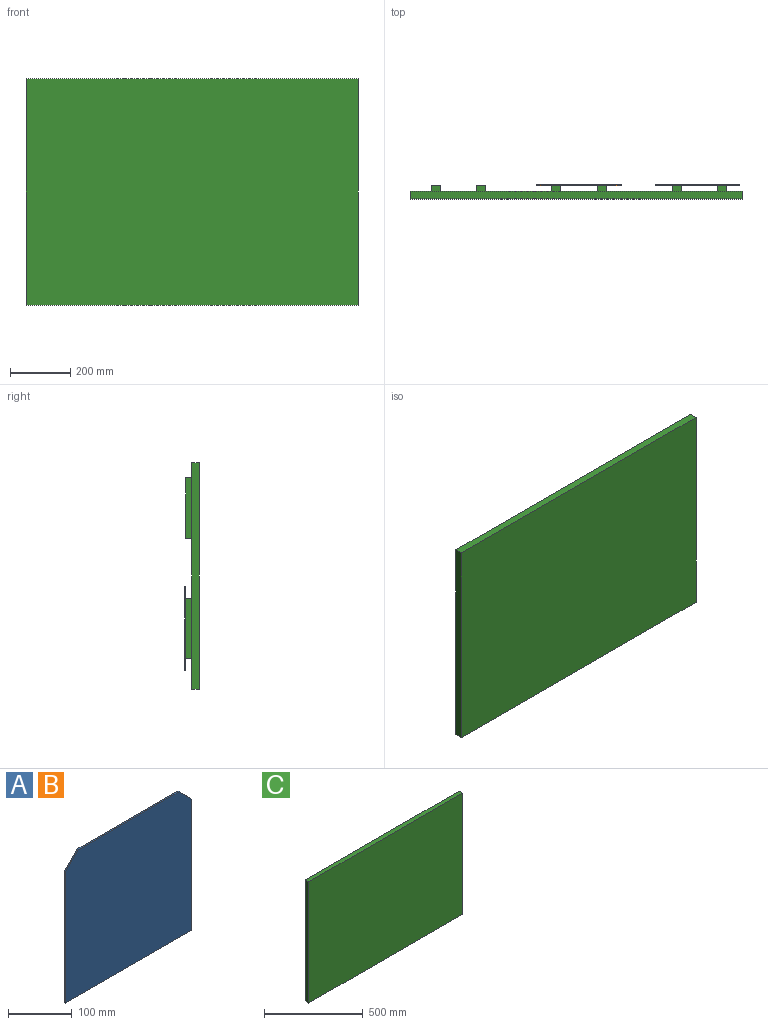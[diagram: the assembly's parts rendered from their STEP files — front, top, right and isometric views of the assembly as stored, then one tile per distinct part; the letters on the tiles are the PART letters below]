
ASSEMBLY  parts=3 mates=2
PART A: 8 faces, bbox 280x3x280 mm
  f0: plane 280x3mm, normal (0,0,-1), area 840mm2, adj f1,f5,f6,f7
  f1: plane 251.72x3mm, normal (1,0,0), area 755.1mm2, adj f0,f2,f6,f7
  f2: plane 28.28x28.28mm, normal (0.71,0,0.71), area 120mm2, adj f1,f3,f6,f7
  f3: plane 223.43x3mm, normal (0,0,1), area 670.3mm2, adj f2,f4,f6,f7
  f4: plane 28.28x28.28mm, normal (-0.71,0,0.71), area 120mm2, adj f3,f5,f6,f7
  f5: plane 251.72x3mm, normal (-1,0,0), area 755.1mm2, adj f0,f4,f6,f7
  f6: plane 280x280mm, normal (0,-1,0), area 77600mm2, adj f0,f1,f2,f3,f4,f5
  f7: plane 280x280mm, normal (0,1,0), area 77600mm2, adj f0,f1,f2,f3,f4,f5
PART B: same geometry as A
PART C: 66 faces, bbox 1100x45x750 mm
  f0: plane 200x20mm, normal (1,0,0), area 4000mm2, adj f1,f3,f4,f10
  f1: plane 30x20mm, normal (0,0,-1), area 600mm2, adj f0,f2,f4,f10
  f2: plane 200x20mm, normal (-1,0,0), area 4000mm2, adj f1,f3,f4,f10
  f3: plane 30x20mm, normal (0,0,1), area 600mm2, adj f0,f2,f4,f10
  f4: plane 200x30mm, normal (0,1,0), area 6000mm2, adj f0,f1,f2,f3
  f5: plane 750x25mm, normal (-1,0,0), area 18750mm2, adj f6,f8,f9,f10
  f6: plane 1100x25mm, normal (0,0,-1), area 27500mm2, adj f5,f7,f9,f10
  f7: plane 750x25mm, normal (1,0,0), area 18750mm2, adj f6,f8,f9,f10
  f8: plane 1100x25mm, normal (0,0,1), area 27500mm2, adj f5,f7,f9,f10
  f9: plane 1100x750mm, normal (0,-1,0), area 825000mm2, adj f5,f6,f7,f8
  f10: plane 1100x750mm, normal (0,1,0), area 753000mm2, adj f0,f1,f2,f3,f5,f6,f7,f8
  f11: plane 200x20mm, normal (1,0,0), area 4000mm2, adj f10,f12,f14,f15
  f12: plane 30x20mm, normal (0,0,-1), area 600mm2, adj f10,f11,f13,f15
  f13: plane 200x20mm, normal (-1,0,0), area 4000mm2, adj f10,f12,f14,f15
  f14: plane 30x20mm, normal (0,0,1), area 600mm2, adj f10,f11,f13,f15
  f15: plane 200x30mm, normal (0,1,0), area 6000mm2, adj f11,f12,f13,f14
  f16: plane 200x20mm, normal (1,0,0), area 4000mm2, adj f10,f17,f19,f20
  f17: plane 30x20mm, normal (0,0,-1), area 600mm2, adj f10,f16,f18,f20
  f18: plane 200x20mm, normal (-1,0,0), area 4000mm2, adj f10,f17,f19,f20
  f19: plane 30x20mm, normal (0,0,1), area 600mm2, adj f10,f16,f18,f20
  f20: plane 200x30mm, normal (0,1,0), area 6000mm2, adj f16,f17,f18,f19
  f21: plane 200x20mm, normal (1,0,0), area 4000mm2, adj f10,f22,f24,f25
  f22: plane 30x20mm, normal (0,0,-1), area 600mm2, adj f10,f21,f23,f25
  f23: plane 200x20mm, normal (-1,0,0), area 4000mm2, adj f10,f22,f24,f25
  f24: plane 30x20mm, normal (0,0,1), area 600mm2, adj f10,f21,f23,f25
  f25: plane 200x30mm, normal (0,1,0), area 6000mm2, adj f21,f22,f23,f24
  f26: plane 200x20mm, normal (1,0,0), area 4000mm2, adj f10,f27,f29,f30
  f27: plane 30x20mm, normal (0,0,-1), area 600mm2, adj f10,f26,f28,f30
  f28: plane 200x20mm, normal (-1,0,0), area 4000mm2, adj f10,f27,f29,f30
  f29: plane 30x20mm, normal (0,0,1), area 600mm2, adj f10,f26,f28,f30
  f30: plane 200x30mm, normal (0,1,0), area 6000mm2, adj f26,f27,f28,f29
  f31: plane 200x20mm, normal (1,0,0), area 4000mm2, adj f10,f32,f34,f35
  f32: plane 30x20mm, normal (0,0,-1), area 600mm2, adj f10,f31,f33,f35
  f33: plane 200x20mm, normal (-1,0,0), area 4000mm2, adj f10,f32,f34,f35
  f34: plane 30x20mm, normal (0,0,1), area 600mm2, adj f10,f31,f33,f35
  f35: plane 200x30mm, normal (0,1,0), area 6000mm2, adj f31,f32,f33,f34
  f36: plane 200x20mm, normal (1,0,0), area 4000mm2, adj f10,f37,f39,f40
  f37: plane 30x20mm, normal (0,0,-1), area 600mm2, adj f10,f36,f38,f40
  f38: plane 200x20mm, normal (-1,0,0), area 4000mm2, adj f10,f37,f39,f40
  f39: plane 30x20mm, normal (0,0,1), area 600mm2, adj f10,f36,f38,f40
  f40: plane 200x30mm, normal (0,1,0), area 6000mm2, adj f36,f37,f38,f39
  f41: plane 200x20mm, normal (1,0,0), area 4000mm2, adj f10,f42,f44,f45
  f42: plane 30x20mm, normal (0,0,-1), area 600mm2, adj f10,f41,f43,f45
  f43: plane 200x20mm, normal (-1,0,0), area 4000mm2, adj f10,f42,f44,f45
  f44: plane 30x20mm, normal (0,0,1), area 600mm2, adj f10,f41,f43,f45
  f45: plane 200x30mm, normal (0,1,0), area 6000mm2, adj f41,f42,f43,f44
  f46: plane 200x20mm, normal (1,0,0), area 4000mm2, adj f10,f47,f49,f50
  f47: plane 30x20mm, normal (0,0,-1), area 600mm2, adj f10,f46,f48,f50
  f48: plane 200x20mm, normal (-1,0,0), area 4000mm2, adj f10,f47,f49,f50
  f49: plane 30x20mm, normal (0,0,1), area 600mm2, adj f10,f46,f48,f50
  f50: plane 200x30mm, normal (0,1,0), area 6000mm2, adj f46,f47,f48,f49
  f51: plane 200x20mm, normal (1,0,0), area 4000mm2, adj f10,f52,f54,f55
  f52: plane 30x20mm, normal (0,0,-1), area 600mm2, adj f10,f51,f53,f55
  f53: plane 200x20mm, normal (-1,0,0), area 4000mm2, adj f10,f52,f54,f55
  f54: plane 30x20mm, normal (0,0,1), area 600mm2, adj f10,f51,f53,f55
  f55: plane 200x30mm, normal (0,1,0), area 6000mm2, adj f51,f52,f53,f54
  f56: plane 200x20mm, normal (1,0,0), area 4000mm2, adj f10,f57,f59,f60
  f57: plane 30x20mm, normal (0,0,-1), area 600mm2, adj f10,f56,f58,f60
  f58: plane 200x20mm, normal (-1,0,0), area 4000mm2, adj f10,f57,f59,f60
  f59: plane 30x20mm, normal (0,0,1), area 600mm2, adj f10,f56,f58,f60
  f60: plane 200x30mm, normal (0,1,0), area 6000mm2, adj f56,f57,f58,f59
  f61: plane 200x20mm, normal (1,0,0), area 4000mm2, adj f10,f62,f64,f65
  f62: plane 30x20mm, normal (0,0,-1), area 600mm2, adj f10,f61,f63,f65
  f63: plane 200x20mm, normal (-1,0,0), area 4000mm2, adj f10,f62,f64,f65
  f64: plane 30x20mm, normal (0,0,1), area 600mm2, adj f10,f61,f63,f65
  f65: plane 200x30mm, normal (0,1,0), area 6000mm2, adj f61,f62,f63,f64
PLACE A t=(226.75,194.01,-30.35)mm
PLACE B t=(-165.25,194.01,-30.35)mm
PLACE C t=(-585.25,171.01,-91.7)mm
MATE planar A.f6 <-> C.f45  axis (0,-1,0) through (366.75,191.01,108.3)mm
MATE planar B.f6 <-> C.f55  axis (0,-1,0) through (-25.25,191.01,108.3)mm
